# Revit family: 2093155 Accessories_Sylvania_MC2 HORIZ-CORNER_Ceiling Surface
name_source: partatom
category: Generic Models
revit_build: Autodesk Revit 2015 (Build: 20140606_1530(x64)
units: mm (PartAtom-declared; Revit-internal decimal feet)

## types (1)
- MC2 90º HORIZ-CORNER WHT OPAL
    Catalog Number = 2093155 MC2 90º HORIZ-CORNER WHT OPAL
    Corner Material = Metal_Sylvania_Mini Continuum_White
    Default Elevation = 0 mm  [stored 0 ft]
    Description = Used to conect two mini continuum luminaires together
    Diffuser Material = Polycarbonate_Mini Continuum_Opal
    Height = 86 mm  [stored 0.282152 ft]
    Manufacturer = Feilo Sylvania
    Model = MC2 90º HORIZ-CORNER WHT OPAL
    Offset = 40 mm  [stored 0.131234 ft]
    Product Family = MINI CONTINUUM II-ACCESSORIES
    Product Page URL = http://www.feilosylvania.com
    URL = http://www.feilosylvania.com
    Weight = 0.50 kg
    Width = 54 mm  [stored 0.177165 ft]

note: [stored X ft] marks values corroborated as IEEE doubles in the binary element streams (Revit-internal decimal feet)

## geometry (parser evidence)
native form markers: Sweep x3
no freeform markers — native parametric forms only
